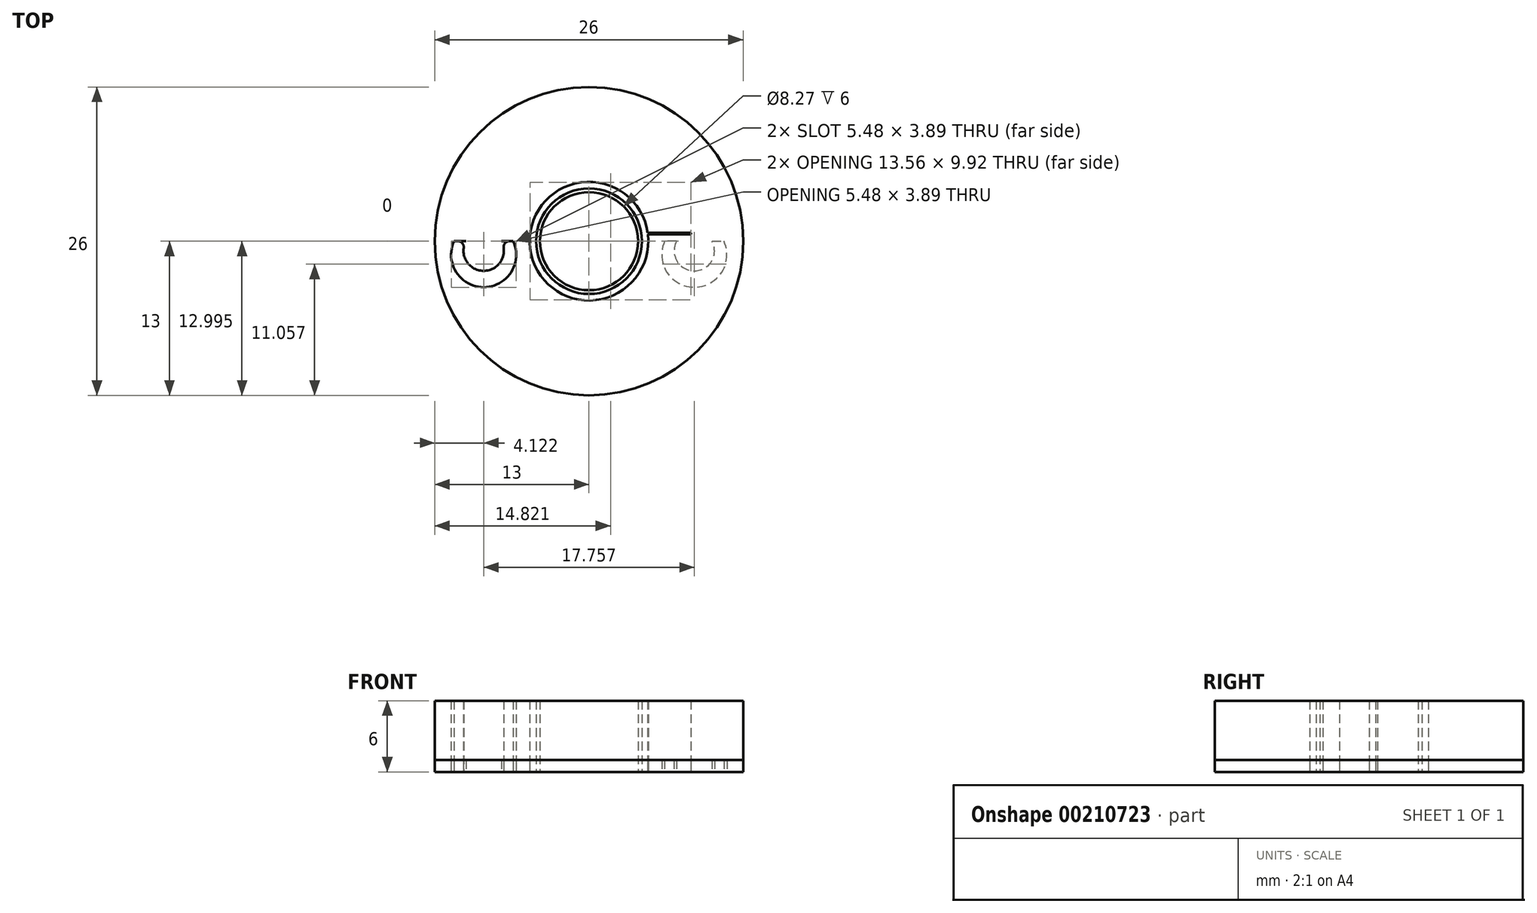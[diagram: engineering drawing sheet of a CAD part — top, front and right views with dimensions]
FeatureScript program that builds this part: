
annotation { "Feature Type Name" : "Feature", "Feature Type Description" : "" }
export const myFeature = defineFeature(function(context is Context, id is Id, definition is map)
    precondition{}
    {
        {
            var Q0;
            Q0=qCreatedBy(makeId("Top.planeOp"),FACE);
            var sketch = newSketch(context, id + "F0", { "sketchPlane" : qUnion([Q0])});
            skCircle(sketch, "E0", {"center": v(0, 0) * mm, "radius": 13 * mm});
            skCircle(sketch, "E1", {"center": v(0, 0) * mm, "radius": 5 * mm});
            skArc(sketch, "E2", {"start": v(7.38, 0) * mm, "mid": v(8.88, -2.5) * mm, "end": v(10.38, 0) * mm});
            skArc(sketch, "E3", {"start": v(8.6, 0.57) * mm, "mid": v(8.88, -2.2) * mm, "end": v(9.16, 0.57) * mm});
            skCircle(sketch, "E4", {"center": v(0, 0) * mm, "radius": 4.45 * mm});
            skLineSegment(sketch, "E5.left", {"start": v(8.6, 0.57) * mm, "end": v(8.6, 0.71) * mm});
            skLineSegment(sketch, "E5.right", {"start": v(9.16, 0.57) * mm, "end": v(9.16, 1.07) * mm});
            skLineSegment(sketch, "E6", {"start": v(8.88, 0.82) * mm, "end": v(8.88, -0.8) * mm});
            skPoint(sketch, "E6.startSnap0", {"position": v(9.16, 0.82) * mm});
            skPoint(sketch, "E6.startSnap1", {"position": v(8.88, -2.2) * mm});
            skArc(sketch, "E7", {"start": v(9.16, 1.07) * mm, "mid": v(8.87, 3.85) * mm, "end": v(8.6, 1.07) * mm});
            skLineSegment(sketch, "E8", {"start": v(8.88, 0.82) * mm, "end": v(8.88, 2.45) * mm});
            skLineSegment(sketch, "E9", {"start": v(0, 0) * mm, "end": v(0, -2.27) * mm});
            skCircle(sketch, "E10", {"center": v(0, 0) * mm, "radius": 4.14 * mm});
            skLineSegment(sketch, "E11.bottom", {"start": v(8.6, 0.71) * mm, "end": v(4.4, 0.71) * mm});
            skLineSegment(sketch, "E11.top", {"start": v(8.6, 0.57) * mm, "end": v(4.42, 0.57) * mm});
            skLineSegment(sketch, "E11.left", {"start": v(8.6, 0.71) * mm, "end": v(8.6, 0.57) * mm});
            skPoint(sketch, "E12", {"position": v(4.42, 0.57) * mm});
            skPoint(sketch, "E13", {"position": v(4.4, 0.71) * mm});
            skPoint(sketch, "E11.right.end.orphan", {"position": v(4.1, 0.57) * mm});
            skPoint(sketch, "E14.orphan", {"position": v(-12.36, 4.04) * mm});
            skPoint(sketch, "E15.orphan", {"position": v(-12.4, -4.04) * mm});
            skPoint(sketch, "E16.orphan", {"position": v(12.38, 0) * mm});
            skPoint(sketch, "E17.orphan", {"position": v(-12.38, 0) * mm});
            skPoint(sketch, "E18.end.orphan", {"position": v(-7.38, 0) * mm});
            skPoint(sketch, "E18.start.orphan", {"position": v(-10.38, 0) * mm});
            skArc(sketch, "E19.MirrorCS", {"start": v(-7.38, 0) * mm, "mid": v(-8.88, -2.5) * mm, "end": v(-10.38, 0) * mm});
            skLineSegment(sketch, "E20", {"start": v(-10.38, 0) * mm, "end": v(-11.38, 0) * mm});
            skLineSegment(sketch, "E21", {"start": v(-7.38, 0) * mm, "end": v(-6.38, 0) * mm});
            skArc(sketch, "E22", {"start": v(-11.38, 0) * mm, "mid": v(-8.88, -3.89) * mm, "end": v(-6.38, 0) * mm});
            skArc(sketch, "E23.MirrorCS", {"start": v(11.38, 0) * mm, "mid": v(8.88, -3.89) * mm, "end": v(6.38, 0) * mm});
            skLineSegment(sketch, "E24.MirrorCS", {"start": v(7.38, 0) * mm, "end": v(6.38, 0) * mm});
            skLineSegment(sketch, "E25", {"start": v(10.38, 0) * mm, "end": v(11.38, 0) * mm});
            skLineSegment(sketch, "E26.trimOffspring", {"start": v(12.4, 3.92) * mm, "end": v(12.4, 4.04) * mm});
            skPoint(sketch, "E27.left.start.orphan", {"position": v(12.36, -4.04) * mm});
            skLineSegment(sketch, "E28.trimOffspring", {"start": v(6.38, 0) * mm, "end": v(7.38, 0) * mm});
            skSolve(sketch);
        }
        {
            var Q0;
            Q0=makeQuery(id+"F0.imprint","IMPRINT",FACE,{"disambiguationData":[TD([[makeQuery(id+"F0.imprint","IMPRINT",EDGE,{"derivedFrom":sQuery(id+"F0.wireOp",EDGE,"E19.MirrorCS")}),1.0]])]});
            var Q1;
            Q1=makeQuery(id+"F0.imprint","IMPRINT",FACE,{"disambiguationData":[TD([[makeQuery(id+"F0.imprint","IMPRINT",EDGE,{"derivedFrom":sQuery(id+"F0.wireOp",EDGE,"E2")}),-1.0]])]});
            extrude(context, id + "F1", {"entities" : qUnion([Q0, Q1]), "depth" : 6 * mm});
        }
        {
            var Q0;
            Q0=makeQuery(id+"F0.imprint","IMPRINT",FACE,{"disambiguationData":[TD([[makeQuery(id+"F0.imprint","IMPRINT",EDGE,{"derivedFrom":sQuery(id+"F0.wireOp",EDGE,"E0")}),1.0]])]});
            extrude(context, id + "F2", {"entities" : qUnion([Q0]), "depth" : 1 * mm});
        }
        {
            var Q0;
            Q0=makeQuery(id+"F0.imprint","IMPRINT",FACE,{"disambiguationData":[TD([[makeQuery(id+"F0.imprint","IMPRINT",EDGE,{"derivedFrom":sQuery(id+"F0.wireOp",EDGE,"E10")}),-1.0]])]});
            extrude(context, id + "F3", {"entities" : qUnion([Q0]), "depth" : 6 * mm});
        }
        {
            var Q0;
            Q0=makeQuery(id+"F1.opExtrude","SWEPT_EDGE",EDGE,{"disambiguationData":[OSD([sQuery(id+"F0.wireOp",EDGE,"E2"),sQuery(id+"F0.wireOp",EDGE,"E28.trimOffspring")])]});
            var Q1;
            Q1=makeQuery(id+"F1.opExtrude","SWEPT_EDGE",EDGE,{"disambiguationData":[OSD([sQuery(id+"F0.wireOp",EDGE,"E2"),sQuery(id+"F0.wireOp",EDGE,"E25")])]});
            var Q2;
            Q2=makeQuery(id+"F1.opExtrude","SWEPT_EDGE",EDGE,{"disambiguationData":[OSD([sQuery(id+"F0.wireOp",EDGE,"E19.MirrorCS"),sQuery(id+"F0.wireOp",EDGE,"E21")])]});
            var Q3;
            Q3=makeQuery(id+"F1.opExtrude","SWEPT_EDGE",EDGE,{"disambiguationData":[OSD([sQuery(id+"F0.wireOp",EDGE,"E19.MirrorCS"),sQuery(id+"F0.wireOp",EDGE,"E20")])]});
            fillet(context, id + "F4", {"entities" : qUnion([Q0, Q1, Q2, Q3]), "radius" : .5 * mm, "tangentPropagation" : true, "allowEdgeOverflow" : false});
        }
    });
